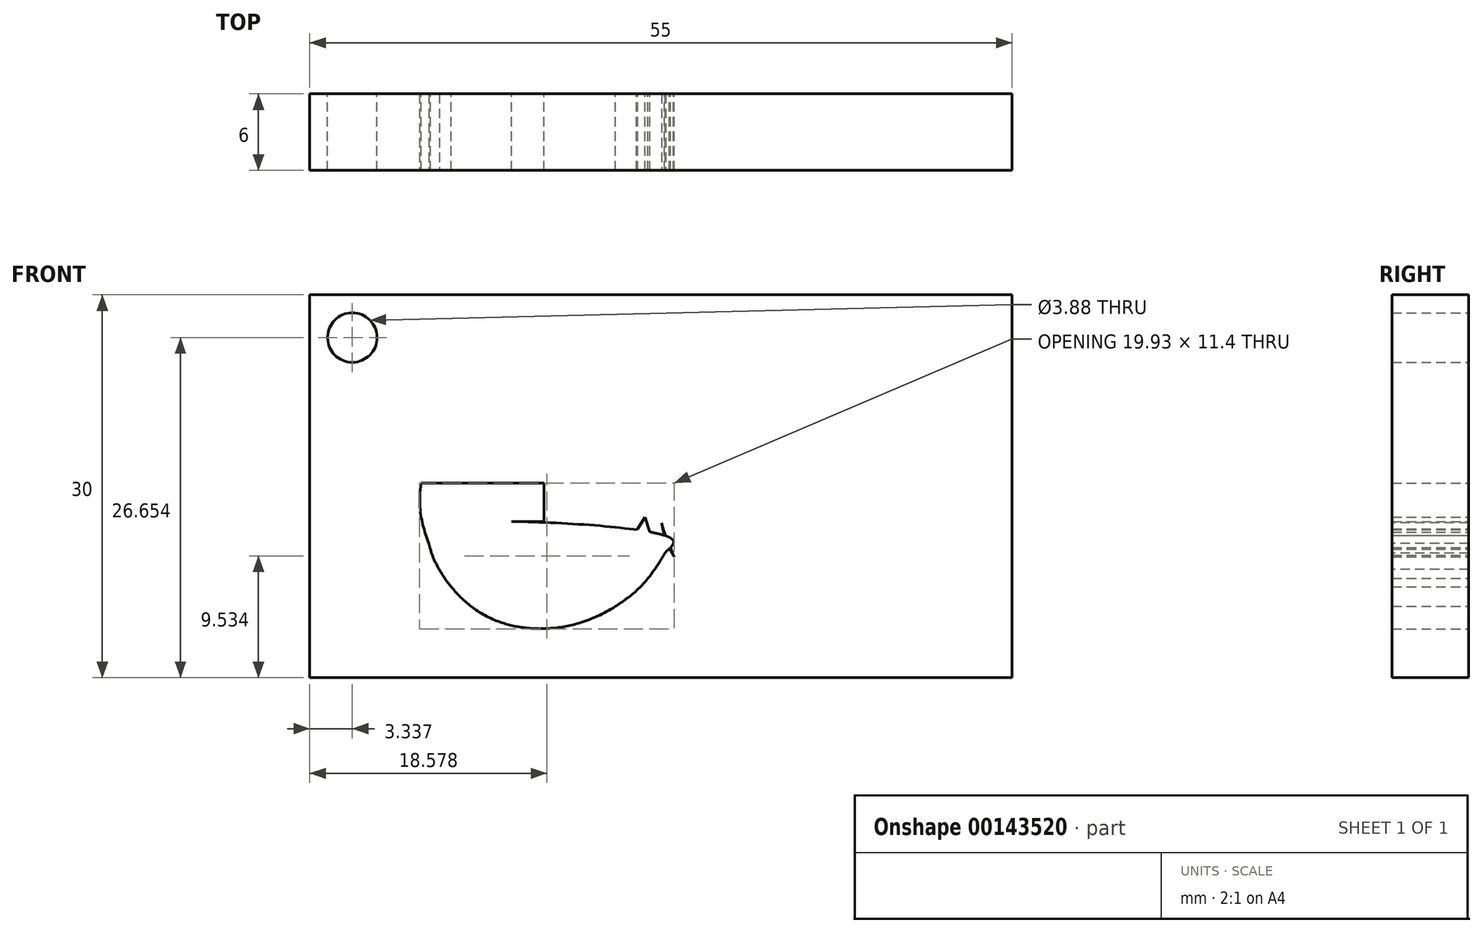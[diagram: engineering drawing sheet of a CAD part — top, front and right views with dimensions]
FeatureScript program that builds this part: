
annotation { "Feature Type Name" : "Feature", "Feature Type Description" : "" }
export const myFeature = defineFeature(function(context is Context, id is Id, definition is map)
    precondition{}
    {
        {
            var Q0;
            Q0=qCreatedBy(makeId("Front.planeOp"),FACE);
            var sketch = newSketch(context, id + "F0", { "sketchPlane" : qUnion([Q0])});
            skLineSegment(sketch, "E0.bottom", {"start": v(27.5, -15) * mm, "end": v(-27.5, -15) * mm});
            skLineSegment(sketch, "E0.top", {"start": v(27.5, 15) * mm, "end": v(-27.5, 15) * mm});
            skLineSegment(sketch, "E0.left", {"start": v(27.5, -15) * mm, "end": v(27.5, 15) * mm});
            skLineSegment(sketch, "E0.right", {"start": v(-27.5, -15) * mm, "end": v(-27.5, 15) * mm});
            skArc(sketch, "E1", {"start": v(22.9, 8.37) * mm, "mid": v(15.8, 12.93) * mm, "end": v(7.45, 11.7) * mm});
            skArc(sketch, "E2.trimOffspring", {"start": v(-1.8, 10.48) * mm, "mid": v(-10.69, 12.24) * mm, "end": v(-17.66, 6.48) * mm});
            skFitSpline(sketch, "E3", {"points": [v(-1.8, 10.48) * mm, v(2.84, 3.27) * mm, v(4.05, -4.6) * mm], "startDerivative": vector(16, -12.2) * mm, "endDerivative": vector(11.47, -15.86) * mm});
            skLineSegment(sketch, "E4", {"start": v(0.48, -4.25) * mm, "end": v(0.48, -4.25) * mm});
            skArc(sketch, "E5.0", {"start": v(-3.61, 8.08) * mm, "mid": v(-9.96, 9.33) * mm, "end": v(-14.95, 5.2) * mm});
            skFitSpline(sketch, "E5.1", {"points": [v(-3.63, 8.1) * mm, v(-3.07, 7.67) * mm, v(-2.1, 6.8) * mm, v(-1.23, 5.72) * mm, v(-0.73, 4.87) * mm, v(-0.45, 4.25) * mm, v(-0.29, 3.74) * mm, v(-0.2, 3.33) * mm, v(-0.15, 3.03) * mm, v(-0.12, 2.72) * mm, v(-0.1, 2.37) * mm, v(-0.1, 1.97) * mm, v(-0.11, 1.39) * mm, v(-0.15, 0.55) * mm, v(-0.17, -0.6) * mm, v(-0.1, -1.9) * mm, v(0.15, -3.34) * mm, v(0.68, -4.87) * mm, v(1.26, -5.87) * mm, v(1.61, -6.35) * mm]});
            skFitSpline(sketch, "E6", {"points": [v(7.45, 11.7) * mm, v(2.36, 7.98) * mm], "startDerivative": vector(-10.78, -6.14) * mm, "endDerivative": vector(-2.85, -2.22) * mm});
            skArc(sketch, "E7.0", {"start": v(21, 5.83) * mm, "mid": v(16.02, 9.77) * mm, "end": v(9.68, 9.46) * mm});
            skFitSpline(sketch, "E8.0", {"points": [v(8.94, 9.1) * mm, v(8.1, 8.62) * mm, v(7.13, 8.02) * mm, v(6.28, 7.4) * mm, v(5.81, 7.03) * mm, v(5.44, 6.7) * mm, v(5.1, 6.4) * mm, v(4.72, 6.03) * mm, v(4.39, 5.75) * mm, v(4.2, 5.6) * mm]});
            skFitSpline(sketch, "E9", {"points": [v(4.05, -4.6) * mm, v(11.8, -8.54) * mm, v(21.74, -6.34) * mm], "startDerivative": vector(15.2, -12.77) * mm, "endDerivative": vector(16.74, 9.92) * mm});
            skFitSpline(sketch, "E10.0", {"points": [v(2.11, -6.89) * mm, v(2.8, -7.46) * mm, v(4.18, -8.56) * mm, v(6.07, -9.75) * mm, v(7.72, -10.53) * mm, v(9.03, -11.02) * mm, v(10.18, -11.32) * mm, v(11.13, -11.49) * mm, v(12.11, -11.6) * mm, v(13.34, -11.67) * mm, v(15.32, -11.59) * mm, v(17.78, -11.18) * mm, v(20.64, -10.28) * mm, v(22.42, -9.42) * mm, v(23.27, -8.92) * mm]});
            skFitSpline(sketch, "E11", {"points": [v(0.53, -4.1) * mm, v(2.18, -6.94) * mm], "startDerivative": vector(0.73, -4.3) * mm, "endDerivative": vector(2.81, -2.1) * mm});
            skFitSpline(sketch, "E12", {"points": [v(8.16, 8.64) * mm, v(9.68, 9.46) * mm], "startDerivative": vector(1.52, 0.82) * mm, "endDerivative": vector(1.52, 0.82) * mm});
            skFitSpline(sketch, "E13", {"points": [v(-1.84, -2.8) * mm, v(-10.02, -7.98) * mm, v(-15.43, -2.77) * mm], "startDerivative": vector(-10.56, -21.33) * mm, "endDerivative": vector(-2.93, 20.52) * mm});
            skFitSpline(sketch, "E14.0", {"points": [v(0.85, -4.12) * mm, v(0.3, -5.24) * mm, v(-1.03, -7.22) * mm, v(-3.57, -9.41) * mm, v(-6.47, -10.74) * mm, v(-9.53, -11.17) * mm, v(-12.56, -10.66) * mm, v(-14.88, -9.4) * mm, v(-16.42, -7.88) * mm, v(-17.36, -6.5) * mm, v(-18.05, -4.94) * mm, v(-18.31, -3.79) * mm, v(-18.4, -3.2) * mm, v(0.85, -4.12) * mm]});
            skFitSpline(sketch, "E15.0", {"points": [v(0.85, -4.12) * mm, v(0.3, -5.24) * mm, v(-1.03, -7.22) * mm, v(-3.57, -9.41) * mm, v(-6.47, -10.74) * mm, v(-9.53, -11.17) * mm, v(-12.56, -10.66) * mm, v(-14.88, -9.4) * mm, v(-16.42, -7.88) * mm, v(-17.36, -6.5) * mm, v(-18.05, -4.94) * mm, v(-18.31, -3.79) * mm, v(-18.4, -3.2) * mm]});
            skLineSegment(sketch, "E16", {"start": v(-18.84, 0.23) * mm, "end": v(-9.14, 0.23) * mm});
            skLineSegment(sketch, "E17", {"start": v(-9.14, 0.23) * mm, "end": v(-9.14, -2.77) * mm});
            skLineSegment(sketch, "E18", {"start": v(-9.14, -2.77) * mm, "end": v(-15.43, -2.77) * mm});
            skFitSpline(sketch, "E19", {"points": [v(5.26, 6.54) * mm, v(3.52, 5.08) * mm], "startDerivative": vector(-1.74, -1.46) * mm, "endDerivative": vector(-1.74, -1.46) * mm});
            skLineSegment(sketch, "E20", {"start": v(2.36, 7.98) * mm, "end": v(3.52, 5.08) * mm});
            skLineSegment(sketch, "E21", {"start": v(21, 5.83) * mm, "end": v(22.9, 8.37) * mm});
            skLineSegment(sketch, "E22", {"start": v(21.74, -6.34) * mm, "end": v(23.27, -8.92) * mm});
            skLineSegment(sketch, "E23", {"start": v(-14.95, 5.2) * mm, "end": v(-17.66, 6.48) * mm});
            skLineSegment(sketch, "E24", {"start": v(-1.8, 10.48) * mm, "end": v(0.91, 8.4) * mm});
            skLineSegment(sketch, "E25", {"start": v(-1.84, -3.33) * mm, "end": v(-2.67, -4.21) * mm});
            skLineSegment(sketch, "E26", {"start": v(-2.67, -4.21) * mm, "end": v(-1.84, -3.33) * mm});
            skLineSegment(sketch, "E27", {"start": v(-1.84, -3.33) * mm, "end": v(-1.25, -2.43) * mm});
            skLineSegment(sketch, "E28", {"start": v(-1.25, -2.43) * mm, "end": v(-0.14, -5.73) * mm});
            skLineSegment(sketch, "E29", {"start": v(0.48, -4.25) * mm, "end": v(0.62, -4.56) * mm});
            skLineSegment(sketch, "E30", {"start": v(-14.2, -9.7) * mm, "end": v(-14.2, -9.7) * mm});
            skLineSegment(sketch, "E31", {"start": v(-0.8, -6.71) * mm, "end": v(-0.8, -6.71) * mm});
            skFitSpline(sketch, "E32", {"points": [v(-18.79, 0.23) * mm, v(-17.81, -5.42) * mm], "startDerivative": vector(-1.12, -7.22) * mm, "endDerivative": vector(1.86, -4.87) * mm});
            skLineSegment(sketch, "E33", {"start": v(-0.14, -5.73) * mm, "end": v(-0.8, -6.71) * mm});
            skPoint(sketch, "E34.start.orphan", {"position": v(-14, 0.23) * mm});
            skLineSegment(sketch, "E35", {"start": v(7.22, -10.29) * mm, "end": v(7.22, -10.29) * mm});
            skFitSpline(sketch, "E36", {"points": [v(-0.07, -1.96) * mm, v(0.77, -5.1) * mm, v(4.14, -8.47) * mm], "startDerivative": vector(0.82, -6.97) * mm, "endDerivative": vector(7.57, -5.52) * mm});
            skLineSegment(sketch, "E37", {"start": v(0.77, -5.1) * mm, "end": v(0.86, -5.08) * mm});
            skFitSpline(sketch, "E38", {"points": [v(-0.09, -1.8) * mm, v(0.97, -5.42) * mm], "startDerivative": vector(0.26, -5.14) * mm, "endDerivative": vector(1.06, -3.56) * mm});
            skCircle(sketch, "E39", {"center": v(-24.16, 11.65) * mm, "radius": 1.94 * mm});
            skSolve(sketch);
        }
        {
            var Q0;
            Q0=makeQuery(id+"F0.imprint","IMPRINT",FACE,{"disambiguationData":[TD([[makeQuery(id+"F0.imprint","IMPRINT",EDGE,{"derivedFrom":sQuery(id+"F0.wireOp",EDGE,"E0.bottom")}),-1.0]])]});
            extrude(context, id + "F1", {"entities" : qUnion([Q0]), "endBound" : BoundingType.SYMMETRIC, "depth" : 6 * mm});
        }
    });
